# Revit family: Запорный клапан Strömax 4215 W, муфта х муфта
name_source: partatom
category: Rohrzubehör
revit_build: Autodesk Revit 2018 (Build: 20190510_1515(x64)
units: mm (PartAtom-declared; Revit-internal decimal feet)

## family parameters
Arbeitsebenenbasiert = Nein
Beim Laden mit Abzugskörper schneiden = Nein
Bemaßung runder Anschluss = Durchmesser verwenden
Gemeinsam genutzt = Nein
Immer vertikal = Ja
OmniClass-Nummer = 23.65.55.14
OmniClass-Titel = Valves for Liquid Services
Teiletyp = Unterbricht

## types (1)
- Запорный клапан Strömax 4215 W, муфта х муфта
    H04 = 21 mm  [stored 0.0688976 ft]
    Hersteller = HERZ Armaturen Ges.m.b.H.
    L02 = 12 mm  [stored 0.0393701 ft]
    O-Ring = EPDM
    R07 = 3 mm  [stored 0.00984252 ft]
    S03 = 60 mm  [stored 0.19685 ft]
    SCTWCODE = 04;01;02
    SCTWSEQ = FW;SBT_TYP_FW="106";2
    SC_NennweiteBerechnet = 0
    URL = www.herz-armaturen.ru
    Корпус = латунь, устойчивая к селективной цинковой коррозии, в соответствии с EN1982
    Макс. перепад давления на закрытом седле = 1000000.0 Pa
    Макс. рабочая температура = 90 °C
    Макс. рабочее давление = 1000000.0 Pa
    Маховик = пластик, цвет маховика - зеленый
    Область применения = Для перекрытия трубопроводов в системе питьевого водоснабжения в зданиях.
    Примечание = В соответствии со статьей 33 Регламента REACH (Registration; Evaluation; Authorisation; Restriction of Chemicals) (EC № 1907/2006) мы обязаны указать, что свинец внесен в список SVHC (Substances of Very High Concern - вещества очень высокой важности) и весовой процент свинца во всех латунных компонентах заводского изготовления в наших изделиях, превышает 0,1 % (w/w) (CAS: 7439-92-1 / EINECS: 231-100-4).
Поскольку свинец является легирующим компонентом сплава, прямое негативное влияние исключается, и поэтому дополнительной информации о безопасном использовании не требуется.
    Среда = Питьевая вода

note: [stored X ft] marks values corroborated as IEEE doubles in the binary element streams (Revit-internal decimal feet)
